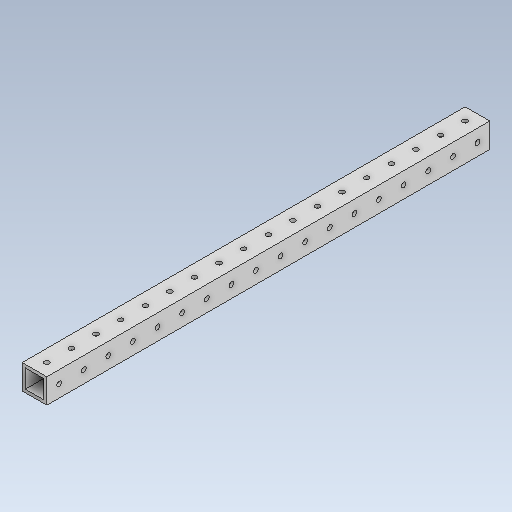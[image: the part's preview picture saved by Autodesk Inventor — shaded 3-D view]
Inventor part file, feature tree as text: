
AUTODESK INVENTOR PART (.ipt)
format: ipt  version: 2020 (Build 240168000, 168)  size: 194,560 bytes
history: native  units: in
note: dims shown in document units (in); Inventor stores cm internally (conversion verified against a paired STEP export)
features: other x3, sketch x3
ambient origin geometry x8: Origin, YZ Plane, XZ Plane, XY Plane, X Axis, Y Axis, Z Axis, Center Point
bodies: Solid1 (feature_tree)
feature tree (6):
  other  "1x1x18.ipt"
  other  "Solid1::1x1x18.ipt"
  other  "TaggingFeature1"
  sketch  "Sketch1"  dims[d0=0.3937in]
  sketch  "Sketch2"
  sketch  "Sketch3"
